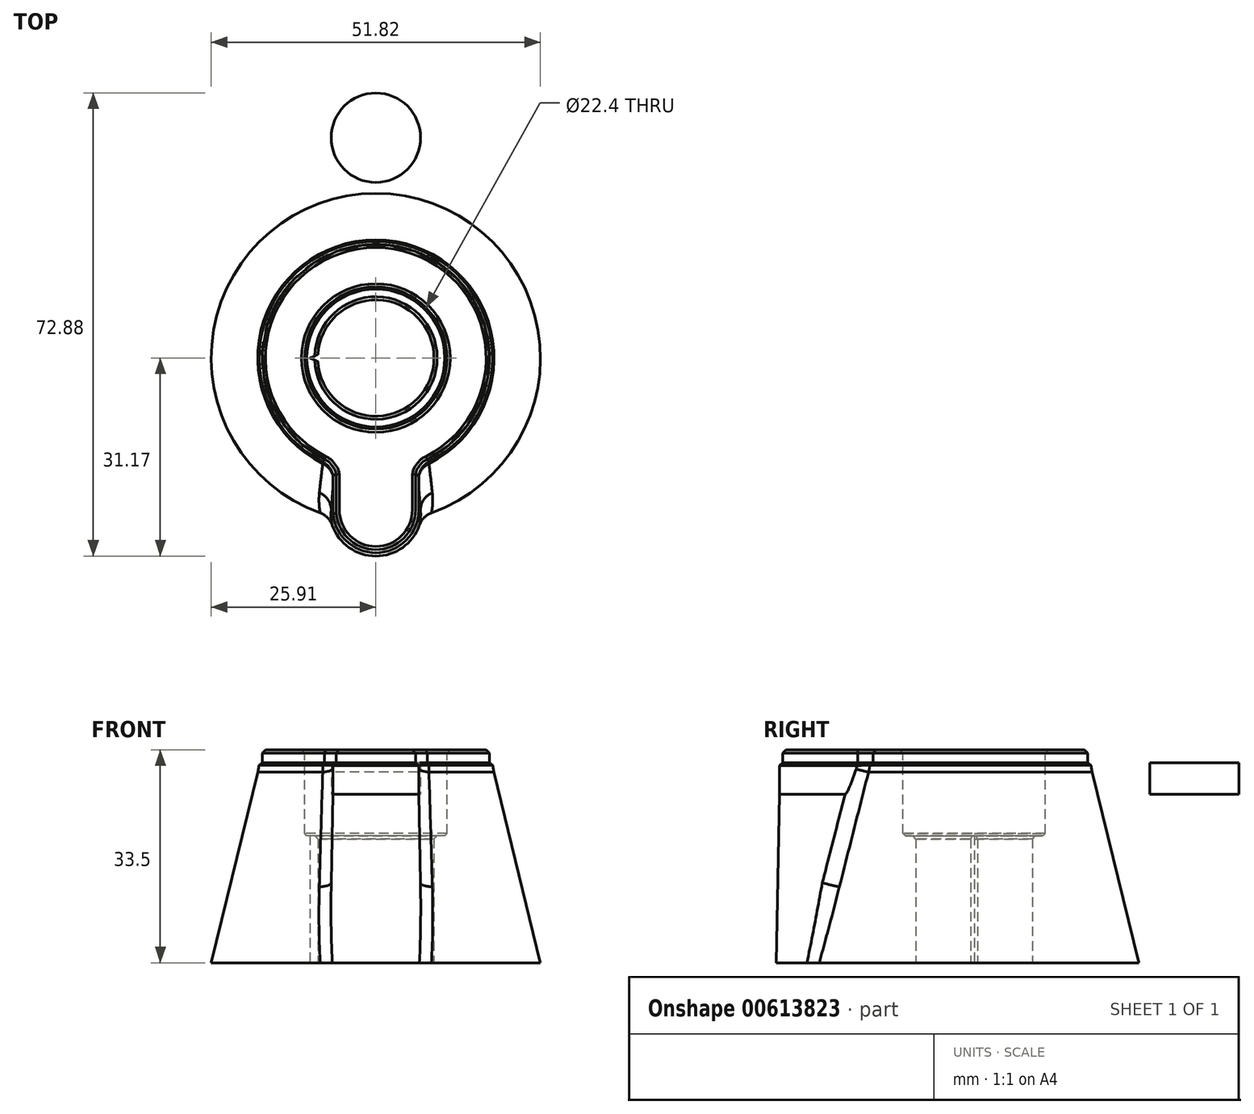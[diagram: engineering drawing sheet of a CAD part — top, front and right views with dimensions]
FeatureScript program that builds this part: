
annotation { "Feature Type Name" : "Feature", "Feature Type Description" : "" }
export const myFeature = defineFeature(function(context is Context, id is Id, definition is map)
    precondition{}
    {
        {
            var Q0;
            Q0=qCreatedBy(makeId("Top.planeOp"),FACE);
            var sketch = newSketch(context, id + "F0", { "sketchPlane" : qUnion([Q0])});
            skCircle(sketch, "E0", {"center": v(0, 0) * mm, "radius": 27.12 * mm});
            skSolve(sketch);
        }
        {
            var Q0;
            Q0=qCreatedBy(makeId("Top.planeOp"),FACE);
            cPlane(context, id + "F1", {"entities" : qUnion([Q0]), "cplaneType" : CPlaneType.OFFSET, "offset" : 35 * mm, "width" : 150 * mm, "height" : 150 * mm});
        }
        {
            var Q0;
            Q0=qCreatedBy(id+"F1.planeOp",FACE);
            var sketch = newSketch(context, id + "F2", { "sketchPlane" : qUnion([Q0])});
            skCircle(sketch, "E1", {"center": v(0, 0) * mm, "radius": 18.6 * mm});
            skSolve(sketch);
        }
        {
            var Q0;
            Q0=makeQuery(id+"F0.imprint","IMPRINT",FACE,{"disambiguationData":[TD([[makeQuery(id+"F0.imprint","IMPRINT",EDGE,{"derivedFrom":sQuery(id+"F0.wireOp",EDGE,"E0")}),1.0]])]});
            var Q1;
            Q1=makeQuery(id+"F2.imprint","IMPRINT",FACE,{"disambiguationData":[TD([[makeQuery(id+"F2.imprint","IMPRINT",EDGE,{"derivedFrom":sQuery(id+"F2.wireOp",EDGE,"E1")}),1.0]])]});
            loft(context, id + "F3", {"sheetProfilesArray" : [{ "sheetProfileEntities" : qUnion([Q0]) }, { "sheetProfileEntities" : qUnion([Q1]) }]});
        }
        {
            var Q0;
            Q0=makeQuery(id+"F3.opLoft","CAP_FACE",FACE,{"disambiguationData":[OSD([makeQuery(id+"F0.imprint","IMPRINT",FACE,{"disambiguationData":[TD([[makeQuery(id+"F0.imprint","IMPRINT",EDGE,{"derivedFrom":sQuery(id+"F0.wireOp",EDGE,"E0")}),1.0]])]})])],"isStart":true});
            var sketch = newSketch(context, id + "F4", { "sketchPlane" : qUnion([Q0])});
            skCircle(sketch, "E2", {"center": v(0, 0) * mm, "radius": 9.15 * mm});
            skSolve(sketch);
        }
        {
            var Q0;
            Q0 = qSketchRegion(id + "F4", true);
            extrude(context, id + "F5", {"entities" : qUnion([Q0]), "operationType" : NewBodyOperationType.REMOVE, "endBound" : BoundingType.THROUGH_ALL, "oppositeDirection" : true, "depth" : 25 * mm, "offsetDistance" : 25 * mm});
        }
        {
            var Q0;
            Q0=makeQuery(id+"F3.opLoft","CAP_FACE",FACE,{"disambiguationData":[OSD([makeQuery(id+"F2.imprint","IMPRINT",FACE,{"disambiguationData":[TD([[makeQuery(id+"F2.imprint","IMPRINT",EDGE,{"derivedFrom":sQuery(id+"F2.wireOp",EDGE,"E1")}),1.0]])]})])],"isStart":true});
            var sketch = newSketch(context, id + "F6", { "sketchPlane" : qUnion([Q0])});
            skCircle(sketch, "E3", {"center": v(0, 0) * mm, "radius": 11.35 * mm});
            skSolve(sketch);
        }
        {
            var Q0;
            Q0 = qSketchRegion(id + "F6", true);
            extrude(context, id + "F7", {"entities" : qUnion([Q0]), "operationType" : NewBodyOperationType.REMOVE, "oppositeDirection" : true, "depth" : 10 * mm, "offsetDistance" : 25 * mm});
        }
        {
            var Q0;
            Q0=makeQuery(id+"F7.boolean.opBoolean","COPY",EDGE,{"derivedFrom":makeQuery(id+"F7.opExtrude","CAP_EDGE",EDGE,{"disambiguationData":[OSD([sQuery(id+"F6.wireOp",EDGE,"E3")])],"isStart":false})});
            var Q1;
            Q1=makeQuery(id+"F7.boolean.opBoolean","INTERSECT",EDGE,{"derivedFrom":[makeQuery(id+"F5.boolean.opBoolean","COPY",FACE,{"derivedFrom":makeQuery(id+"F5.opExtrude","SWEPT_FACE",FACE,{"disambiguationData":[OSD([sQuery(id+"F4.wireOp",EDGE,"E2")])]})}),makeQuery(id+"F7.opExtrude","CAP_FACE",FACE,{"disambiguationData":[OSD([sQuery(id+"F6.wireOp",EDGE,"E3")])],"isStart":false})]});
            chamfer(context, id + "F8", {"entities" : qUnion([Q0, Q1]), "width" : 0.5 * mm, "tangentPropagation" : true});
        }
        {
            var Q0;
            Q0=makeQuery(id+"F3.opLoft","CAP_FACE",FACE,{"disambiguationData":[OSD([makeQuery(id+"F0.imprint","IMPRINT",FACE,{"disambiguationData":[TD([[makeQuery(id+"F0.imprint","IMPRINT",EDGE,{"derivedFrom":sQuery(id+"F0.wireOp",EDGE,"E0")}),1.0]])]})])],"isStart":true});
            cPlane(context, id + "F9", {"entities" : qUnion([Q0]), "cplaneType" : CPlaneType.OFFSET, "offset" : 30 * mm, "width" : 150 * mm, "height" : 150 * mm});
        }
        {
            var Q0;
            Q0=qCreatedBy(id+"F9.planeOp",FACE);
            var sketch = newSketch(context, id + "F10", { "sketchPlane" : qUnion([Q0])});
            skArc(sketch, "E4", {"start": v(7.95, 23.9) * mm, "mid": v(0, 31.85) * mm, "end": v(-7.95, 23.9) * mm});
            skLineSegment(sketch, "E5", {"start": v(-7.95, 23.9) * mm, "end": v(-7.95, 15) * mm});
            skLineSegment(sketch, "E6", {"start": v(-7.95, 15) * mm, "end": v(7.95, 15) * mm});
            skLineSegment(sketch, "E7", {"start": v(7.95, 15) * mm, "end": v(7.95, 23.9) * mm});
            skSolve(sketch);
        }
        {
            var Q0;
            Q0=qCreatedBy(id+"F9.planeOp",FACE);
            cPlane(context, id + "F11", {"entities" : qUnion([Q0]), "cplaneType" : CPlaneType.OFFSET, "offset" : 61.5 * mm, "oppositeDirection" : true, "width" : 150 * mm, "height" : 150 * mm});
        }
        {
            var Q0;
            Q0=qCreatedBy(id+"F11.planeOp",FACE);
            var sketch = newSketch(context, id + "F12", { "sketchPlane" : qUnion([Q0])});
            skArc(sketch, "E8", {"start": v(6.75, 23.9) * mm, "mid": v(0, 30.65) * mm, "end": v(-6.75, 23.9) * mm});
            skLineSegment(sketch, "E9", {"start": v(6.75, 23.9) * mm, "end": v(6.75, 13.9) * mm});
            skLineSegment(sketch, "E10", {"start": v(6.75, 13.9) * mm, "end": v(-6.75, 13.9) * mm});
            skLineSegment(sketch, "E11", {"start": v(-6.75, 13.9) * mm, "end": v(-6.75, 23.9) * mm});
            skSolve(sketch);
        }
        {
            var Q1;
            Q1=makeQuery(id+"F10.imprint","IMPRINT",FACE,{"disambiguationData":[TD([[makeQuery(id+"F10.imprint","IMPRINT",EDGE,{"derivedFrom":sQuery(id+"F10.wireOp",EDGE,"E4")}),1.0]])]});
            var Q2;
            Q2=makeQuery(id+"F12.imprint","IMPRINT",FACE,{"disambiguationData":[TD([[makeQuery(id+"F12.imprint","IMPRINT",EDGE,{"derivedFrom":sQuery(id+"F12.wireOp",EDGE,"E8")}),1.0]])]});
            loft(context, id + "F13", {"operationType" : NewBodyOperationType.ADD, "sheetProfilesArray" : [{ "sheetProfileEntities" : qUnion([Q1]) }, { "sheetProfileEntities" : qUnion([Q2]) }]});
        }
        {
            var Q0;
            Q0=makeQuery(id+"F3.opLoft","CAP_FACE",FACE,{"disambiguationData":[OSD([makeQuery(id+"F0.imprint","IMPRINT",FACE,{"disambiguationData":[TD([[makeQuery(id+"F0.imprint","IMPRINT",EDGE,{"derivedFrom":sQuery(id+"F0.wireOp",EDGE,"E0")}),1.0]])]})])],"isStart":true});
            var sketch = newSketch(context, id + "F14", { "sketchPlane" : qUnion([Q0])});
            skCircle(sketch, "E12", {"center": v(0, 0) * mm, "radius": 44.91 * mm});
            skSolve(sketch);
        }
        {
            var Q0;
            Q0 = qSketchRegion(id + "F14", true);
            extrude(context, id + "F15", {"entities" : qUnion([Q0]), "operationType" : NewBodyOperationType.REMOVE, "endBound" : BoundingType.THROUGH_ALL, "depth" : 25 * mm, "offsetDistance" : 25 * mm});
        }
        {
            var Q0;
            Q0=makeQuery(id+"F13.opLoft","CAP_FACE",FACE,{"disambiguationData":[OSD([makeQuery(id+"F12.imprint","IMPRINT",FACE,{"disambiguationData":[TD([[makeQuery(id+"F12.imprint","IMPRINT",EDGE,{"derivedFrom":sQuery(id+"F12.wireOp",EDGE,"E8")}),1.0]])]})])],"isStart":true});
            var sketch = newSketch(context, id + "F16", { "sketchPlane" : qUnion([Q0])});
            skCircle(sketch, "E13", {"center": v(0, 0) * mm, "radius": 46.82 * mm});
            skSolve(sketch);
        }
        {
            var Q0;
            Q0=makeQuery(id+"F15.boolean.opBoolean","MERGE",FACE,{"derivedFrom":[makeQuery(id+"F3.opLoft","CAP_FACE",FACE,{"disambiguationData":[OSD([makeQuery(id+"F0.imprint","IMPRINT",FACE,{"disambiguationData":[TD([[makeQuery(id+"F0.imprint","IMPRINT",EDGE,{"derivedFrom":sQuery(id+"F0.wireOp",EDGE,"E0")}),1.0]])]})])],"isStart":true}),makeQuery(id+"F15.opExtrude","CAP_FACE",FACE,{"disambiguationData":[OSD([sQuery(id+"F14.wireOp",EDGE,"E12")])],"isStart":true})]});
            var sketch = newSketch(context, id + "F17", { "sketchPlane" : qUnion([Q0])});
            skLineSegment(sketch, "E14", {"start": v(-9.13, 0.55) * mm, "end": v(-10.38, 0) * mm});
            skLineSegment(sketch, "E15", {"start": v(-10.38, 0) * mm, "end": v(-9.13, -0.55) * mm});
            skLineSegment(sketch, "E16", {"start": v(-9.13, -0.55) * mm, "end": v(-9.13, 0.55) * mm});
            skLineSegment(sketch, "E17", {"start": v(-9.13, 0) * mm, "end": v(-10.38, 0) * mm, "construction": true});
            skSolve(sketch);
        }
        {
            var Q0;
            Q0=qCreatedBy(makeId("Front.planeOp"),FACE);
            var sketch = newSketch(context, id + "F18", { "sketchPlane" : qUnion([Q0])});
            skLineSegment(sketch, "E18", {"start": v(0, 0) * mm, "end": v(0, 16.76) * mm, "construction": true});
            skSolve(sketch);
        }
        {
            var Q0;
            Q0 = qSketchRegion(id + "F17", true);
            extrude(context, id + "F19", {"entities" : qUnion([Q0]), "operationType" : NewBodyOperationType.REMOVE, "endBound" : BoundingType.THROUGH_ALL, "oppositeDirection" : true, "depth" : 25 * mm, "offsetDistance" : 25 * mm});
        }
        {
            var Q0;
            {var subQ0=sQuery(id+"F12.wireOp",EDGE,"E11");var subQ1=sQuery(id+"F12.wireOp",EDGE,"E9");var subQ2=sQuery(id+"F12.wireOp",EDGE,"E8");Q0=makeQuery(id+"F16.imprint","IMPRINT",FACE,{"disambiguationData":[TD([[makeQuery(id+"F16.imprint","IMPRINT",EDGE,{"derivedFrom":makeQuery(id+"F13.opLoft","MID_CAP_EDGE",EDGE,{"disambiguationData":[OSD([subQ2,subQ1,subQ0])],"capPos":1.0})}),1.0]])]});}
            var sketch = newSketch(context, id + "F20", { "sketchPlane" : qUnion([Q0])});
            skLineSegment(sketch, "E19.0.1", {"start": v(-6.75, -18.24) * mm, "end": v(-6.75, -23.9) * mm});
            skArc(sketch, "E19.0.2", {"start": v(-6.75, -23.9) * mm, "mid": v(0, -30.65) * mm, "end": v(6.75, -23.9) * mm});
            skLineSegment(sketch, "E19.0.3", {"start": v(6.75, -23.9) * mm, "end": v(6.75, -18.24) * mm});
            skLineSegment(sketch, "E20", {"start": v(6.75, -18.24) * mm, "end": v(6.75, -15.14) * mm});
            skLineSegment(sketch, "E21", {"start": v(6.75, -15.14) * mm, "end": v(-6.75, -15.14) * mm});
            skLineSegment(sketch, "E22", {"start": v(-6.75, -15.14) * mm, "end": v(-6.75, -18.24) * mm});
            skSolve(sketch);
        }
        {
            var Q0;
            Q0=makeQuery(id+"F15.boolean.opBoolean","MERGE",FACE,{"derivedFrom":[makeQuery(id+"F3.opLoft","CAP_FACE",FACE,{"disambiguationData":[OSD([makeQuery(id+"F0.imprint","IMPRINT",FACE,{"disambiguationData":[TD([[makeQuery(id+"F0.imprint","IMPRINT",EDGE,{"derivedFrom":sQuery(id+"F0.wireOp",EDGE,"E0")}),1.0]])]})])],"isStart":true}),makeQuery(id+"F15.opExtrude","CAP_FACE",FACE,{"disambiguationData":[OSD([sQuery(id+"F14.wireOp",EDGE,"E12")])],"isStart":true})]});
            var sketch = newSketch(context, id + "F21", { "sketchPlane" : qUnion([Q0])});
            skCircle(sketch, "E23", {"center": v(0, 0) * mm, "radius": 42.12 * mm});
            skSolve(sketch);
        }
        {
            var Q0;
            Q0 = qSketchRegion(id + "F21", true);
            extrude(context, id + "F22", {"entities" : qUnion([Q0]), "operationType" : NewBodyOperationType.REMOVE, "oppositeDirection" : true, "depth" : 2 * mm, "offsetDistance" : 25 * mm});
        }
        {
            var Q0;
            Q0=makeQuery(id+"F16.imprint","IMPRINT",FACE,{"disambiguationData":[TD([[makeQuery(id+"F16.imprint","IMPRINT",EDGE,{"derivedFrom":sQuery(id+"F16.wireOp",EDGE,"E13")}),1.0]])]});
            var sketch = newSketch(context, id + "F23", { "sketchPlane" : qUnion([Q0])});
            skCircle(sketch, "E24", {"center": v(0, 34.68) * mm, "radius": 7.03 * mm});
            skSolve(sketch);
        }
        {
            var Q0;
            Q0 = qSketchRegion(id + "F23", true);
            extrude(context, id + "F24", {"entities" : qUnion([Q0]), "depth" : 5 * mm, "offsetDistance" : 25 * mm});
        }
        {
            var Q0;
            {var subQ0=makeQuery(id+"F2.imprint","IMPRINT",FACE,{"disambiguationData":[TD([[makeQuery(id+"F2.imprint","IMPRINT",EDGE,{"derivedFrom":sQuery(id+"F2.wireOp",EDGE,"E1")}),1.0]])]});Q0=makeQuery(id+"F29.boolean.opBoolean","MERGE",FACE,{"derivedFrom":[makeQuery(id+"F3.opLoft","CAP_FACE",FACE,{"disambiguationData":[OSD([subQ0])],"isStart":true}),makeQuery(id+"F29.opExtrude","CAP_FACE",FACE,{"disambiguationData":[OSD([subQ0])],"isStart":false})]});}
            var sketch = newSketch(context, id + "F25", { "sketchPlane" : qUnion([Q0])});
            skCircle(sketch, "E25", {"center": v(0, 0) * mm, "radius": 18.6 * mm});
            skCircle(sketch, "E26", {"center": v(0, 0) * mm, "radius": 11.35 * mm});
            skSolve(sketch);
        }
        {
            var Q0;
            Q0=makeQuery(id+"F25.imprint","IMPRINT",FACE,{"disambiguationData":[TD([[makeQuery(id+"F25.imprint","IMPRINT",EDGE,{"derivedFrom":sQuery(id+"F25.wireOp",EDGE,"E26")}),-1.0]])]});
            var Q1;
            Q1=makeQuery(id+"F24.opExtrude","CAP_FACE",FACE,{"disambiguationData":[OSD([sQuery(id+"F23.wireOp",EDGE,"E24")])],"isStart":false});
            extrude(context, id + "F26", {"entities" : qUnion([Q0]), "operationType" : NewBodyOperationType.ADD, "endBound" : BoundingType.UP_TO_SURFACE, "depth" : 2 * mm, "endBoundEntityFace" : qUnion([Q1]), "offsetDistance" : 25 * mm, "hasDraft" : true, "draftAngle" : 12 * degree, "draftPullDirection" : true});
        }
        {
            var Q0;
            Q0=makeQuery(id+"F16.imprint","IMPRINT",FACE,{"disambiguationData":[TD([[makeQuery(id+"F16.imprint","IMPRINT",EDGE,{"derivedFrom":sQuery(id+"F16.wireOp",EDGE,"E13")}),1.0]])]});
            var sketch = newSketch(context, id + "F27", { "sketchPlane" : qUnion([Q0])});
            skCircle(sketch, "E27", {"center": v(0, 0) * mm, "radius": 11.35 * mm});
            skCircle(sketch, "E28", {"center": v(0, 0) * mm, "radius": 14.46 * mm});
            skSolve(sketch);
        }
        {
            var Q0;
            Q0 = qSketchRegion(id + "F27", true);
            var Q1;
            Q1=makeQuery(id+"F24.opExtrude","CAP_FACE",FACE,{"disambiguationData":[OSD([sQuery(id+"F23.wireOp",EDGE,"E24")])],"isStart":false});
            extrude(context, id + "F28", {"entities" : qUnion([Q0]), "operationType" : NewBodyOperationType.ADD, "endBound" : BoundingType.UP_TO_SURFACE, "depth" : 25 * mm, "endBoundEntityFace" : qUnion([Q1]), "offsetDistance" : 25 * mm});
        }
        {
            var Q0;
            Q0 = qSketchRegion(id + "F20", true);
            var Q1;
            Q1=makeQuery(id+"F28.boolean.opBoolean","MERGE",FACE,{"derivedFrom":[makeQuery(id+"F26.opExtrude","CAP_FACE",FACE,{"disambiguationData":[OSD([sQuery(id+"F25.wireOp",EDGE,"E25"),sQuery(id+"F25.wireOp",EDGE,"E26")])],"isStart":false}),makeQuery(id+"F28.opExtrude","CAP_FACE",FACE,{"disambiguationData":[OSD([sQuery(id+"F27.wireOp",EDGE,"E27"),sQuery(id+"F27.wireOp",EDGE,"E28")])],"isStart":false})]});
            extrude(context, id + "F29", {"entities" : qUnion([Q0]), "operationType" : NewBodyOperationType.ADD, "endBound" : BoundingType.UP_TO_SURFACE, "depth" : 25 * mm, "endBoundEntityFace" : qUnion([Q1]), "offsetDistance" : 25 * mm});
        }
        {
            var Q0;
            Q0=makeQuery(id+"F13.boolean.opBoolean","INTERSECT",EDGE,{"derivedFrom":[makeQuery(id+"F3.opLoft","SWEPT_FACE",FACE,{"disambiguationData":[OSD([sQuery(id+"F0.wireOp",EDGE,"E0"),sQuery(id+"F2.wireOp",EDGE,"E1")])]}),makeQuery(id+"F13.opLoft","SWEPT_FACE",FACE,{"disambiguationData":[OSD([sQuery(id+"F10.wireOp",EDGE,"E4"),sQuery(id+"F10.wireOp",EDGE,"E6"),sQuery(id+"F10.wireOp",EDGE,"E7"),sQuery(id+"F12.wireOp",EDGE,"E8"),sQuery(id+"F12.wireOp",EDGE,"E9"),sQuery(id+"F12.wireOp",EDGE,"E10")])]})]});
            var Q1;
            Q1=makeQuery(id+"F13.boolean.opBoolean","INTERSECT",EDGE,{"derivedFrom":[makeQuery(id+"F3.opLoft","SWEPT_FACE",FACE,{"disambiguationData":[OSD([sQuery(id+"F0.wireOp",EDGE,"E0"),sQuery(id+"F2.wireOp",EDGE,"E1")])]}),makeQuery(id+"F13.opLoft","SWEPT_FACE",FACE,{"disambiguationData":[OSD([sQuery(id+"F10.wireOp",EDGE,"E4"),sQuery(id+"F10.wireOp",EDGE,"E5"),sQuery(id+"F10.wireOp",EDGE,"E6"),sQuery(id+"F12.wireOp",EDGE,"E8"),sQuery(id+"F12.wireOp",EDGE,"E10"),sQuery(id+"F12.wireOp",EDGE,"E11")])]})]});
            fillet(context, id + "F30", {"entities" : qUnion([Q0, Q1]), "radius" : 3 * mm, "tangentPropagation" : true, "allowEdgeOverflow" : false});
        }
        {
            var Q0;
            Q0=makeQuery(id+"F29.boolean.opBoolean","MERGE",FACE,{"derivedFrom":[makeQuery(id+"F28.boolean.opBoolean","MERGE",FACE,{"derivedFrom":[makeQuery(id+"F26.opExtrude","CAP_FACE",FACE,{"disambiguationData":[OSD([sQuery(id+"F25.wireOp",EDGE,"E25"),sQuery(id+"F25.wireOp",EDGE,"E26")])],"isStart":false}),makeQuery(id+"F28.opExtrude","CAP_FACE",FACE,{"disambiguationData":[OSD([sQuery(id+"F27.wireOp",EDGE,"E27"),sQuery(id+"F27.wireOp",EDGE,"E28")])],"isStart":false})]}),makeQuery(id+"F29.opExtrude","CAP_FACE",FACE,{"disambiguationData":[OSD([sQuery(id+"F20.wireOp",EDGE,"E19.0.1"),sQuery(id+"F20.wireOp",EDGE,"E19.0.2"),sQuery(id+"F20.wireOp",EDGE,"E19.0.3"),sQuery(id+"F20.wireOp",EDGE,"E20"),sQuery(id+"F20.wireOp",EDGE,"E21"),sQuery(id+"F20.wireOp",EDGE,"E22")])],"isStart":false})]});
            chamfer(context, id + "F31", {"entities" : qUnion([Q0]), "width" : 0.5 * mm, "tangentPropagation" : true});
        }
        {
            var Q0;
            Q0=makeQuery(id+"F29.boolean.opBoolean","MERGE",FACE,{"derivedFrom":[makeQuery(id+"F28.boolean.opBoolean","MERGE",FACE,{"derivedFrom":[makeQuery(id+"F26.opExtrude","CAP_FACE",FACE,{"disambiguationData":[OSD([sQuery(id+"F25.wireOp",EDGE,"E25"),sQuery(id+"F25.wireOp",EDGE,"E26")])],"isStart":false}),makeQuery(id+"F28.opExtrude","CAP_FACE",FACE,{"disambiguationData":[OSD([sQuery(id+"F27.wireOp",EDGE,"E27"),sQuery(id+"F27.wireOp",EDGE,"E28")])],"isStart":false})]}),makeQuery(id+"F29.opExtrude","CAP_FACE",FACE,{"disambiguationData":[OSD([sQuery(id+"F20.wireOp",EDGE,"E19.0.1"),sQuery(id+"F20.wireOp",EDGE,"E19.0.2"),sQuery(id+"F20.wireOp",EDGE,"E19.0.3"),sQuery(id+"F20.wireOp",EDGE,"E20"),sQuery(id+"F20.wireOp",EDGE,"E21"),sQuery(id+"F20.wireOp",EDGE,"E22")])],"isStart":false})]});
            var sketch = newSketch(context, id + "F32", { "sketchPlane" : qUnion([Q0])});
            skArc(sketch, "E29.0", {"start": v(8.1, -15.94) * mm, "mid": v(0, 17.88) * mm, "end": v(-8.1, -15.94) * mm});
            skFitSpline(sketch, "E30.0", {"points": [v(-8.1, -15.94) * mm, v(-7.63, -16.17) * mm, v(-7.24, -16.5) * mm, v(-6.9, -16.93) * mm, v(-6.58, -17.36) * mm, v(-6.36, -17.83) * mm, v(-6.25, -18.34) * mm]});
            skLineSegment(sketch, "E30.1", {"start": v(-6.25, -18.34) * mm, "end": v(-6.25, -23.9) * mm});
            skArc(sketch, "E30.2", {"start": v(-6.25, -23.9) * mm, "mid": v(0, -30.15) * mm, "end": v(6.25, -23.9) * mm});
            skLineSegment(sketch, "E30.3", {"start": v(6.25, -23.9) * mm, "end": v(6.25, -18.34) * mm});
            skFitSpline(sketch, "E30.4", {"points": [v(6.25, -18.34) * mm, v(6.36, -17.83) * mm, v(6.58, -17.36) * mm, v(6.9, -16.93) * mm, v(7.23, -16.5) * mm, v(7.63, -16.17) * mm, v(8.1, -15.94) * mm]});
            skSolve(sketch);
        }
        {
            var Q0;
            Q0=makeQuery(id+"F32.imprint","IMPRINT",FACE,{"disambiguationData":[TD([[makeQuery(id+"F32.imprint","IMPRINT",EDGE,{"derivedFrom":sQuery(id+"F32.wireOp",EDGE,"E29.0")}),1.0]])]});
            var sketch = newSketch(context, id + "F33", { "sketchPlane" : qUnion([Q0])});
            skCircle(sketch, "E31.0", {"center": v(0, 0) * mm, "radius": 11.35 * mm});
            skArc(sketch, "E32.0", {"start": v(8.1, -15.94) * mm, "mid": v(0, 17.88) * mm, "end": v(-8.1, -15.94) * mm});
            skFitSpline(sketch, "E32.1", {"points": [v(-8.1, -15.94) * mm, v(-7.63, -16.17) * mm, v(-7.24, -16.5) * mm, v(-6.9, -16.93) * mm, v(-6.58, -17.36) * mm, v(-6.36, -17.83) * mm, v(-6.25, -18.34) * mm]});
            skLineSegment(sketch, "E32.2", {"start": v(-6.25, -18.34) * mm, "end": v(-6.25, -23.9) * mm});
            skArc(sketch, "E32.3", {"start": v(-6.25, -23.9) * mm, "mid": v(0, -30.15) * mm, "end": v(6.25, -23.9) * mm});
            skLineSegment(sketch, "E32.4", {"start": v(6.25, -23.9) * mm, "end": v(6.25, -18.34) * mm});
            skFitSpline(sketch, "E32.5", {"points": [v(6.25, -18.34) * mm, v(6.36, -17.83) * mm, v(6.58, -17.36) * mm, v(6.9, -16.93) * mm, v(7.23, -16.5) * mm, v(7.63, -16.17) * mm, v(8.1, -15.94) * mm]});
            skSolve(sketch);
        }
        {
            var Q0;
            Q0 = qSketchRegion(id + "F33", true);
            extrude(context, id + "F34", {"entities" : qUnion([Q0]), "operationType" : NewBodyOperationType.ADD, "depth" : 2 * mm, "offsetDistance" : 25 * mm, "hasSecondDirection" : true, "secondDirectionOppositeDirection" : true, "secondDirectionDepth" : 0.5 * mm});
        }
        {
            var Q0;
            Q0=makeQuery(id+"F34.opExtrude","CAP_FACE",FACE,{"disambiguationData":[OSD([sQuery(id+"F33.wireOp",EDGE,"E31.0"),sQuery(id+"F33.wireOp",EDGE,"E32.0"),sQuery(id+"F33.wireOp",EDGE,"E32.1"),sQuery(id+"F33.wireOp",EDGE,"E32.2"),sQuery(id+"F33.wireOp",EDGE,"E32.3"),sQuery(id+"F33.wireOp",EDGE,"E32.4"),sQuery(id+"F33.wireOp",EDGE,"E32.5")])],"isStart":false});
            var sketch = newSketch(context, id + "F35", { "sketchPlane" : qUnion([Q0])});
            skCircle(sketch, "E33", {"center": v(0, 0) * mm, "radius": 11.2 * mm});
            skCircle(sketch, "E34", {"center": v(0, 0) * mm, "radius": 12 * mm});
            skSolve(sketch);
        }
        {
            var Q0;
            Q0 = qSketchRegion(id + "F35", true);
            var Q1;
            Q1=makeQuery(id+"F7.boolean.opBoolean","COPY",FACE,{"derivedFrom":makeQuery(id+"F7.opExtrude","CAP_FACE",FACE,{"disambiguationData":[OSD([sQuery(id+"F6.wireOp",EDGE,"E3")])],"isStart":false})});
            extrude(context, id + "F36", {"entities" : qUnion([Q0]), "operationType" : NewBodyOperationType.ADD, "endBound" : BoundingType.UP_TO_SURFACE, "oppositeDirection" : true, "depth" : 25 * mm, "endBoundEntityFace" : qUnion([Q1]), "offsetDistance" : 25 * mm});
        }
        {
            var Q0;
            Q0=makeQuery(id+"F36.boolean.opBoolean","MERGE",FACE,{"derivedFrom":[makeQuery(id+"F34.opExtrude","CAP_FACE",FACE,{"disambiguationData":[OSD([sQuery(id+"F33.wireOp",EDGE,"E31.0"),sQuery(id+"F33.wireOp",EDGE,"E32.0"),sQuery(id+"F33.wireOp",EDGE,"E32.1"),sQuery(id+"F33.wireOp",EDGE,"E32.2"),sQuery(id+"F33.wireOp",EDGE,"E32.3"),sQuery(id+"F33.wireOp",EDGE,"E32.4"),sQuery(id+"F33.wireOp",EDGE,"E32.5")])],"isStart":false}),makeQuery(id+"F36.opExtrude","CAP_FACE",FACE,{"disambiguationData":[OSD([sQuery(id+"F35.wireOp",EDGE,"E33"),sQuery(id+"F35.wireOp",EDGE,"E34")])],"isStart":true})]});
            chamfer(context, id + "F37", {"entities" : qUnion([Q0]), "width" : 0.5 * mm, "tangentPropagation" : true});
        }
        {
            var Q0;
            Q0=makeQuery(id+"F22.boolean.opBoolean","COPY",FACE,{"derivedFrom":makeQuery(id+"F22.opExtrude","CAP_FACE",FACE,{"disambiguationData":[OSD([sQuery(id+"F21.wireOp",EDGE,"E23")])],"isStart":false})});
            var sketch = newSketch(context, id + "F38", { "sketchPlane" : qUnion([Q0])});
            skArc(sketch, "E35.0", {"start": v(8.53, 25.24) * mm, "mid": v(0, -26.64) * mm, "end": v(-8.53, 25.24) * mm});
            skSolve(sketch);
        }
        {
            var Q0;
            Q0=makeQuery(id+"F38.imprint","IMPRINT",FACE,{"disambiguationData":[TD([[makeQuery(id+"F38.imprint","IMPRINT",EDGE,{"derivedFrom":sQuery(id+"F38.wireOp",EDGE,"E35.0")}),-1.0]])]});
            var sketch = newSketch(context, id + "F39", { "sketchPlane" : qUnion([Q0])});
            skCircle(sketch, "E36", {"center": v(0, 0) * mm, "radius": 37.87 * mm});
            skSolve(sketch);
        }
        {
            var Q0;
            Q0 = qSketchRegion(id + "F39", true);
            extrude(context, id + "F40", {"entities" : qUnion([Q0]), "operationType" : NewBodyOperationType.REMOVE, "oppositeDirection" : true, "depth" : 3 * mm, "offsetDistance" : 25 * mm});
        }
    });
